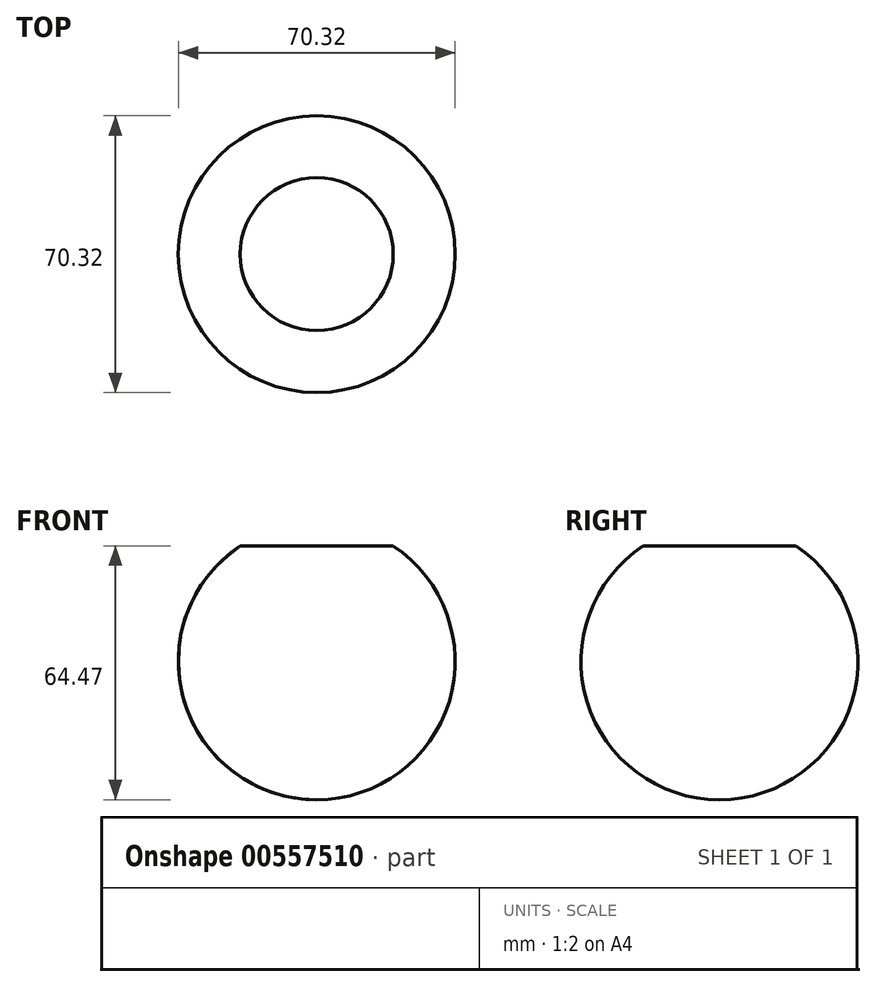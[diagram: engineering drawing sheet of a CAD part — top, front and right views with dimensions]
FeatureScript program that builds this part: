
annotation { "Feature Type Name" : "Feature", "Feature Type Description" : "" }
export const myFeature = defineFeature(function(context is Context, id is Id, definition is map)
    precondition{}
    {
        {
            var Q0;
            Q0=qCreatedBy(makeId("Front.planeOp"),FACE);
            var sketch = newSketch(context, id + "F0", { "sketchPlane" : qUnion([Q0])});
            skArc(sketch, "E0", {"start": v(0, -35.16) * mm, "mid": v(35.16, 0) * mm, "end": v(0, 35.16) * mm});
            skLineSegment(sketch, "E1", {"start": v(0, 47.07) * mm, "end": v(0, -44.4) * mm, "construction": true});
            skLineSegment(sketch, "E2", {"start": v(0, 35.16) * mm, "end": v(0, -35.16) * mm});
            skSolve(sketch);
        }
        {
            var Q0;
            Q0 = qSketchRegion(id + "F0", true);
            var Q1;
            Q1=sQuery(id+"F0.wireOp",EDGE,"E1");
            revolve(context, id + "F1", {"entities" : qUnion([Q0]), "axis" : qUnion([Q1]), "revolveType" : RevolveType.FULL});
        }
        {
            var Q0;
            Q0=qCreatedBy(makeId("Front.planeOp"),FACE);
            var sketch = newSketch(context, id + "F2", { "sketchPlane" : qUnion([Q0])});
            skLineSegment(sketch, "E3.bottom", {"start": v(0, 41.15) * mm, "end": v(25.02, 41.15) * mm});
            skLineSegment(sketch, "E3.top", {"start": v(0, 29.3) * mm, "end": v(25.02, 29.3) * mm});
            skLineSegment(sketch, "E3.left", {"start": v(0, 41.15) * mm, "end": v(0, 29.3) * mm});
            skLineSegment(sketch, "E3.right", {"start": v(25.02, 41.15) * mm, "end": v(25.02, 29.3) * mm});
            skLineSegment(sketch, "E4", {"start": v(0, 51.8) * mm, "end": v(0, -40.56) * mm, "construction": true});
            skPoint(sketch, "E4.endSnap0", {"position": v(0, 35.23) * mm});
            skSolve(sketch);
        }
        {
            var Q0;
            Q0 = qSketchRegion(id + "F2", true);
            var Q1;
            Q1=sQuery(id+"F2.wireOp",EDGE,"E4");
            revolve(context, id + "F3", {"operationType" : NewBodyOperationType.REMOVE, "entities" : qUnion([Q0]), "axis" : qUnion([Q1]), "revolveType" : RevolveType.FULL, "oppositeDirection" : true});
        }
    });
